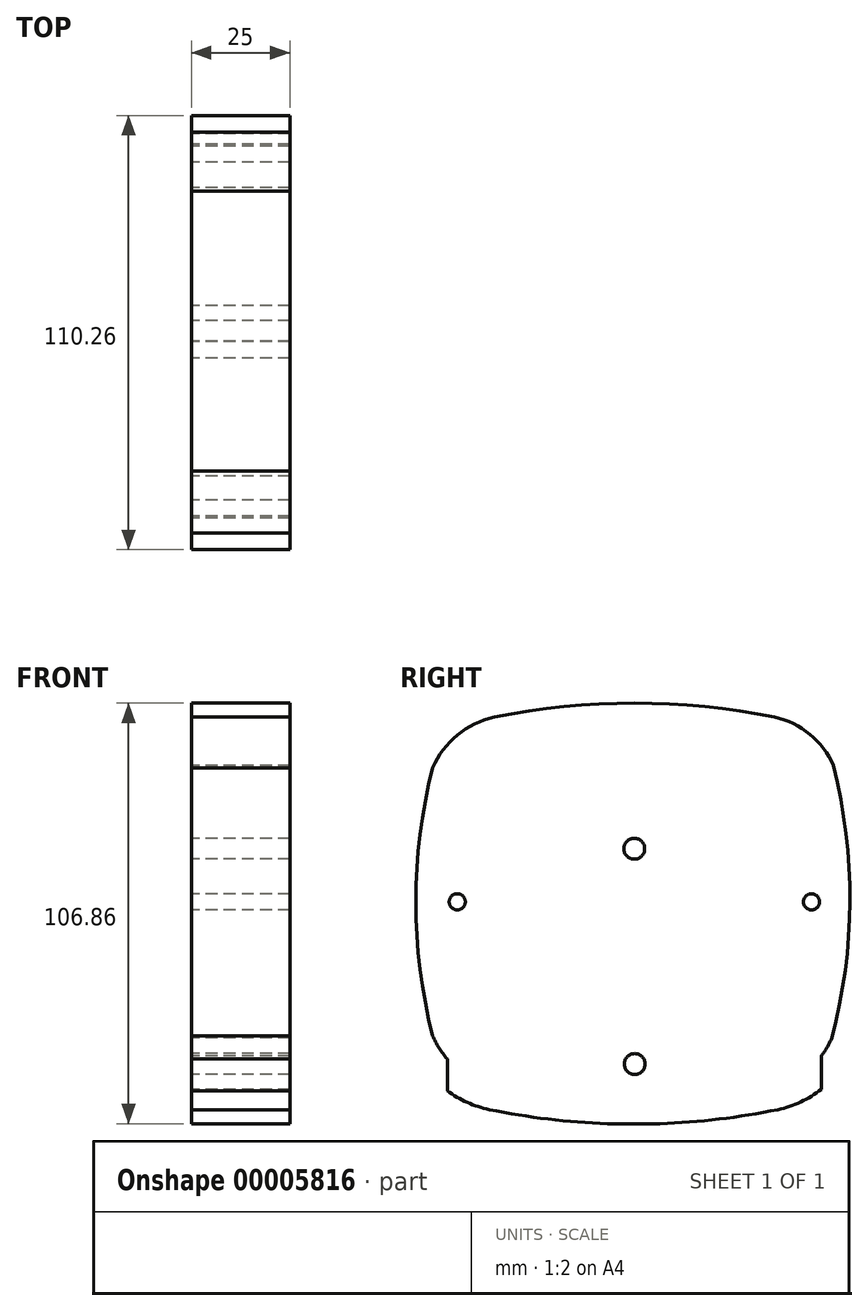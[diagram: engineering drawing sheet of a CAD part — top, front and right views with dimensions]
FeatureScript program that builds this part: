
annotation { "Feature Type Name" : "Feature", "Feature Type Description" : "" }
export const myFeature = defineFeature(function(context is Context, id is Id, definition is map)
    precondition{}
    {
        {
            var Q0;
            Q0=qCreatedBy(makeId("Right.planeOp"),FACE);
            var sketch = newSketch(context, id + "F0", { "sketchPlane" : qUnion([Q0])});
            skLineSegment(sketch, "E0.bottom", {"start": v(0, 42.5) * mm, "end": v(-47.5, 42.5) * mm});
            skLineSegment(sketch, "E0.top", {"start": v(0.17, -42.5) * mm, "end": v(-47.5, -42.5) * mm});
            skLineSegment(sketch, "E0.right", {"start": v(-47.5, 42.5) * mm, "end": v(-47.5, -42.5) * mm});
            skLineSegment(sketch, "E1", {"start": v(0, 0) * mm, "end": v(0.17, -42.5) * mm, "construction": true});
            skLineSegment(sketch, "E2", {"start": v(0, 42.5) * mm, "end": v(0, 0) * mm, "construction": true});
            skLineSegment(sketch, "E3.MirrorCS", {"start": v(47.5, 42.5) * mm, "end": v(47.5, -42.5) * mm});
            skLineSegment(sketch, "E4.MirrorCS", {"start": v(-0.17, -42.5) * mm, "end": v(47.5, -42.5) * mm});
            skLineSegment(sketch, "E5.MirrorCS", {"start": v(0, 42.5) * mm, "end": v(47.5, 42.5) * mm});
            skCircle(sketch, "E6", {"center": v(0, 27.35) * mm, "radius": 2.65 * mm});
            skCircle(sketch, "E7", {"center": v(0.1, -27.35) * mm, "radius": 2.65 * mm});
            skLineSegment(sketch, "E8", {"start": v(-57.95, 13.86) * mm, "end": v(58.83, 13.86) * mm, "construction": true});
            skCircle(sketch, "E9", {"center": v(45.03, 13.86) * mm, "radius": 2.05 * mm});
            skCircle(sketch, "E10", {"center": v(-44.97, 13.86) * mm, "radius": 2.05 * mm});
            skPoint(sketch, "E11", {"position": v(-25.5, 42.5) * mm});
            skPoint(sketch, "E12", {"position": v(0, 42.5) * mm});
            skPoint(sketch, "E13", {"position": v(-47.5, 42.5) * mm});
            skPoint(sketch, "E14", {"position": v(0.03, 13.86) * mm});
            skCircle(sketch, "E15", {"center": v(0.03, 13.86) * mm, "radius": 40 * mm, "construction": true});
            skLineSegment(sketch, "E16.2", {"start": v(-46.28, -25.57) * mm, "end": v(-46.28, -25.58) * mm});
            skLineSegment(sketch, "E17.right", {"start": v(48.47, 46.86) * mm, "end": v(48.47, -19.14) * mm, "construction": true});
            skLineSegment(sketch, "E18.bottom", {"start": v(-34.97, -33.64) * mm, "end": v(35.03, -33.64) * mm, "construction": true});
            skLineSegment(sketch, "E18.top", {"start": v(-34.97, 61.36) * mm, "end": v(35.03, 61.36) * mm, "construction": true});
            skLineSegment(sketch, "E18.left", {"start": v(-34.97, -33.64) * mm, "end": v(-34.97, 61.36) * mm, "construction": true});
            skLineSegment(sketch, "E19", {"start": v(35.03, -33.64) * mm, "end": v(35.03, 61.36) * mm, "construction": true});
            skLineSegment(sketch, "E20", {"start": v(-48.4, 46.86) * mm, "end": v(48.47, 46.86) * mm, "construction": true});
            skLineSegment(sketch, "E21", {"start": v(-48.4, -19.14) * mm, "end": v(48.47, -19.14) * mm, "construction": true});
            skPoint(sketch, "E22", {"position": v(0.03, 61.36) * mm});
            skPoint(sketch, "E23", {"position": v(0.14, -33.64) * mm});
            skPoint(sketch, "E24", {"position": v(52.53, 13.86) * mm});
            skPoint(sketch, "E25", {"position": v(0.03, -33.64) * mm});
            skLineSegment(sketch, "E26", {"start": v(0.03, -42.62) * mm, "end": v(0.03, 13.86) * mm, "construction": true});
            skLineSegment(sketch, "E27", {"start": v(0.03, 13.86) * mm, "end": v(0.03, 61.36) * mm, "construction": true});
            skLineSegment(sketch, "E28", {"start": v(-52.47, 13.86) * mm, "end": v(0.03, 13.86) * mm, "construction": true});
            skPoint(sketch, "E29", {"position": v(-34.97, -19.14) * mm});
            skPoint(sketch, "E30", {"position": v(-34.97, 46.86) * mm});
            skPoint(sketch, "E31", {"position": v(35.03, 46.86) * mm});
            skPoint(sketch, "E32", {"position": v(35.03, -19.14) * mm});
            skLineSegment(sketch, "E33", {"start": v(-34.97, 46.86) * mm, "end": v(35.03, -19.14) * mm, "construction": true});
            skLineSegment(sketch, "E34", {"start": v(35.03, 46.86) * mm, "end": v(-34.97, -19.14) * mm, "construction": true});
            skArc(sketch, "E35.0", {"start": v(-35.58, 60.78) * mm, "mid": v(0.03, 64.36) * mm, "end": v(35.64, 60.78) * mm});
            skArc(sketch, "E35.1", {"start": v(35.64, 60.78) * mm, "mid": v(44.6, 56.44) * mm, "end": v(50.57, 48.48) * mm});
            skArc(sketch, "E35.2", {"start": v(-35.58, 60.78) * mm, "mid": v(-44.97, 56.23) * mm, "end": v(-51.22, 47.88) * mm});
            skArc(sketch, "E35.3", {"start": v(50.18, -20.73) * mm, "mid": v(54.78, 13.85) * mm, "end": v(50.57, 48.48) * mm});
            skArc(sketch, "E35.4", {"start": v(-51.22, 47.88) * mm, "mid": v(-55.48, 13.86) * mm, "end": v(-51.23, -20.16) * mm});
            skArc(sketch, "E35.5", {"start": v(-35.59, -33.06) * mm, "mid": v(-44.98, -28.51) * mm, "end": v(-51.23, -20.16) * mm});
            skArc(sketch, "E35.6", {"start": v(-35.59, -33.06) * mm, "mid": v(-0.18, -36.62) * mm, "end": v(35.23, -33.06) * mm});
            skArc(sketch, "E35.7", {"start": v(35.23, -33.06) * mm, "mid": v(44.2, -28.71) * mm, "end": v(50.18, -20.73) * mm});
            skArc(sketch, "E36.0", {"start": v(-36.8, 66.65) * mm, "mid": v(0.03, 70.36) * mm, "end": v(36.87, 66.65) * mm});
            skArc(sketch, "E36.1", {"start": v(36.87, 66.65) * mm, "mid": v(48.6, 60.92) * mm, "end": v(56.28, 50.39) * mm});
            skArc(sketch, "E36.2", {"start": v(-36.8, 66.65) * mm, "mid": v(-48.96, 60.71) * mm, "end": v(-56.93, 49.79) * mm});
            skArc(sketch, "E36.3", {"start": v(55.87, -22.67) * mm, "mid": v(60.78, 13.83) * mm, "end": v(56.28, 50.39) * mm});
            skArc(sketch, "E36.4", {"start": v(-56.93, 49.79) * mm, "mid": v(-61.48, 13.86) * mm, "end": v(-56.94, -22.07) * mm});
            skArc(sketch, "E36.5", {"start": v(-36.82, -38.94) * mm, "mid": v(-48.97, -33) * mm, "end": v(-56.94, -22.07) * mm});
            skArc(sketch, "E36.6", {"start": v(-36.82, -38.94) * mm, "mid": v(-0.18, -42.62) * mm, "end": v(36.46, -38.94) * mm});
            skArc(sketch, "E36.7", {"start": v(36.46, -38.94) * mm, "mid": v(48.18, -33.2) * mm, "end": v(55.87, -22.67) * mm});
            skSolve(sketch);
        }
        {
            var Q0;
            Q0=makeQuery(id+"F0.imprint","IMPRINT",FACE,{"disambiguationData":[TD([[makeQuery(id+"F0.imprint","IMPRINT",EDGE,{"derivedFrom":sQuery(id+"F0.wireOp",EDGE,"E35.0")}),1.0]])]});
            var Q1;
            {var subQ1=sQuery(id+"F0.wireOp",EDGE,"E35.6");Q1=makeQuery(id+"F0.imprint","IMPRINT",FACE,{"disambiguationData":[TD([[makeQuery(id+"F0.imprint","IMPRINT",EDGE,{"derivedFrom":subQ1}),-1.0]])]});}
            var Q2;
            {var subQ4=sQuery(id+"F0.wireOp",EDGE,"E0.bottom");Q2=makeQuery(id+"F0.imprint","IMPRINT",FACE,{"disambiguationData":[TD([[makeQuery(id+"F0.imprint","IMPRINT",EDGE,{"derivedFrom":subQ4}),1.0]])]});}
            var Q3;
            {var subQ2=sQuery(id+"F0.wireOp",EDGE,"E0.bottom");Q3=makeQuery(id+"F0.imprint","IMPRINT",FACE,{"disambiguationData":[TD([[makeQuery(id+"F0.imprint","IMPRINT",EDGE,{"derivedFrom":subQ2}),-1.0]])]});}
            extrude(context, id + "F1", {"entities" : qUnion([Q0, Q1, Q2, Q3]), "depth" : 25 * mm, "offsetDistance" : 25 * mm});
        }
    });
